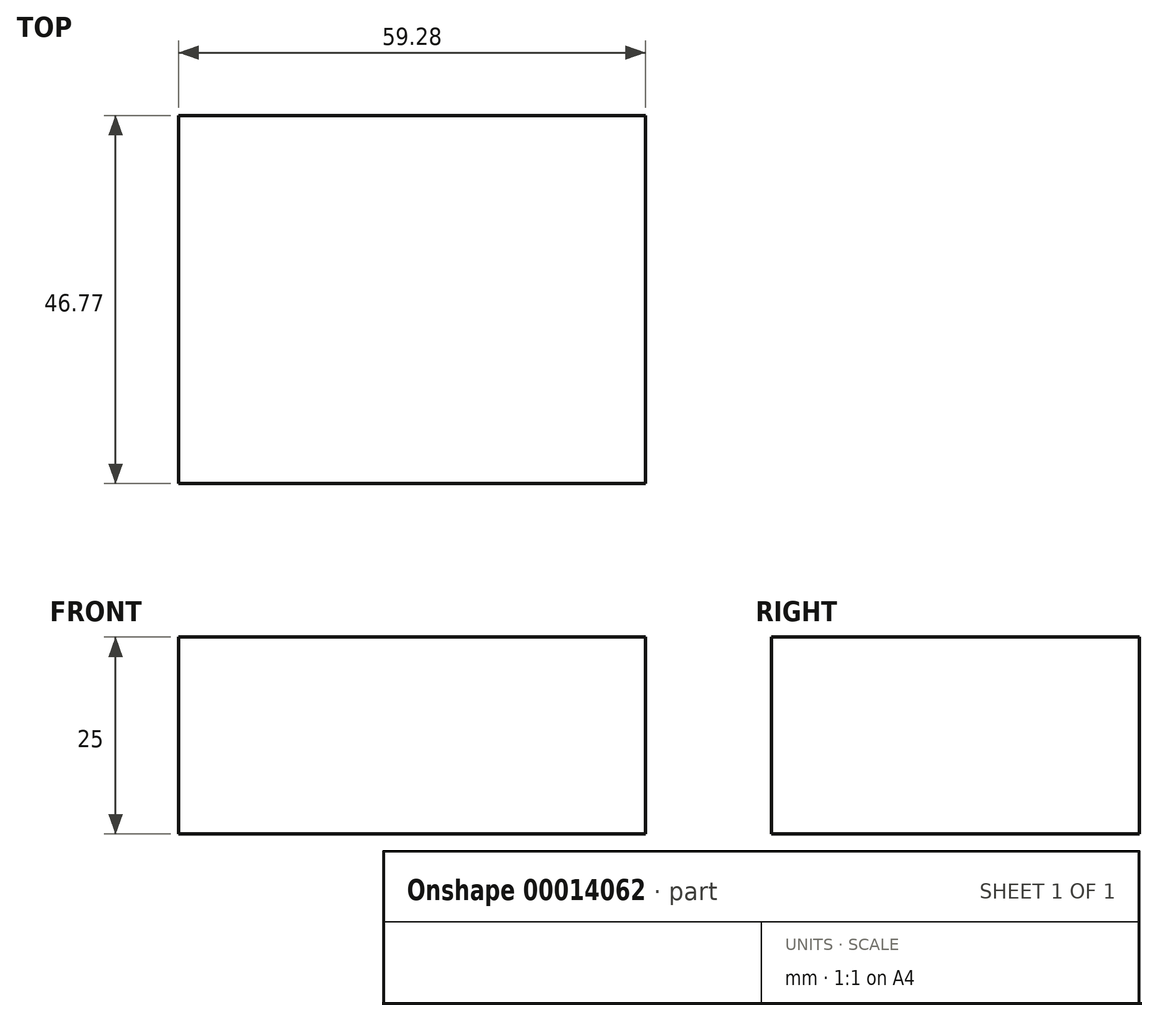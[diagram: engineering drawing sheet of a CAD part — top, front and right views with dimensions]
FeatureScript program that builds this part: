
annotation { "Feature Type Name" : "Feature", "Feature Type Description" : "" }
export const myFeature = defineFeature(function(context is Context, id is Id, definition is map)
    precondition{}
    {
        {
            var Q0;
            Q0=qCreatedBy(makeId("Top.planeOp"),FACE);
            var sketch = newSketch(context, id + "F0", { "sketchPlane" : qUnion([Q0])});
            skLineSegment(sketch, "E0.bottom", {"start": v(0, 0) * mm, "end": v(59.28, 0) * mm});
            skLineSegment(sketch, "E0.top", {"start": v(0, -46.77) * mm, "end": v(59.28, -46.77) * mm});
            skLineSegment(sketch, "E0.left", {"start": v(0, 0) * mm, "end": v(0, -46.77) * mm});
            skLineSegment(sketch, "E0.right", {"start": v(59.28, 0) * mm, "end": v(59.28, -46.77) * mm});
            skSolve(sketch);
        }
        {
            var Q0;
            Q0 = qSketchRegion(id + "F0", true);
            extrude(context, id + "F1", {"entities" : qUnion([Q0]), "depth" : 25 * mm});
        }
    });
